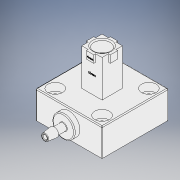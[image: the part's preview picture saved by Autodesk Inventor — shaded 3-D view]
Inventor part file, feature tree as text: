
AUTODESK INVENTOR PART (.ipt)
format: ipt  version: 2019 (Build 230136000, 136)  size: 565,248 bytes
history: native  units: mm
features: sketch x11, extrude x6, plane x3, revolve x2, fillet x2, projected_geometry x2, sweep x1, hole x1, pattern_circular x1
ambient origin geometry x8: Origin, YZ Plane, XZ Plane, XY Plane, X Axis, Y Axis, Z Axis, Center Point
bodies: Solid1 (feature_tree)
feature tree (29):
  revolve  "Revolution1"  [1 undecoded]
  plane  "Work Plane1"
  extrude  "Extrusion1"  Depth=0.75mm
  plane  "Work Plane7"
  extrude  "Extrusion6"  Depth=0.75mm
  extrude  "Extrusion7"  TaperAngle=0.0deg  [1 undecoded]
  sketch  "Sketch17"  dims[d14=2.0mm d15=0.0mm d45=0.0mm d47=15.0mm d48=0.0mm]
  plane  "Work Plane8"
  sweep  "Sweep3"
  fillet  "Fillet1"  Radius=15.0mm
  hole  "Hole3"  [1 undecoded]
  revolve  "Revolution2"  [1 undecoded]
  fillet  "Fillet2"  [1 undecoded]
  extrude  "Extrusion13"  Depth=25.4mm
  pattern_circular  "Circular Pattern1"  [2 undecoded]
  sketch  "Sketch29"  dims[d72=4.496mm d73=6.0mm d74=7.938mm d75=4.166mm d76=90.0deg d77=19.05mm d78=20.594885mm]
  sketch  "Sketch30"  dims[d79=3.0mm d80=6.0mm d81=5.0mm d82=1.8796mm d83=0.25mm d84=2.413mm d85=5.08mm d86=1.15mm d87=0.25mm d88=0.25mm d89=90.0deg d90=0.5mm d124=0.0mm d125=0.0mm d126=4.0mm d127=1.0mm d128=0.0mm d129=40.0mm d130=360.0deg d133=5.5mm d134=1.013632mm d135=0.5mm d136=0.0mm d137=0.5mm d138=0.0mm d139=1.0mm]
  extrude  "Extrusion14"  Depth=5.0mm
  extrude  "Extrusion15"  Depth=1.8796mm
  sketch  "Sketch1"  dims[d1=20.0mm d5=9.0mm]
  sketch  "Sketch2"  dims[d6=0.35mm d7=0.75mm]
  sketch  "Sketch11"  dims[d8=0.75mm d9=0.75mm]
  sketch  "Sketch16"  dims[d10=90.0deg d11=0.0mm]
  projected_geometry  "Projected Loop9"
  sketch  "Sketch18"  dims[d60=36.0mm d61=36.0mm]
  sketch  "Sketch19"  dims[d64=8.45mm d65=32.7mm d66=0.0mm d67=0.0mm d68=0.0mm]
  sketch  "Sketch21"  dims[d69=3.0mm d70=25.4mm]
  sketch  "Sketch28"  dims[d71=25.4mm]
  projected_geometry  "Projected Loop13"
note: 7 required parameter values undecoded (feature->parameter linkage not recoverable at this tier; creation-order binding heuristic only, values carry confidence <= 0.55)